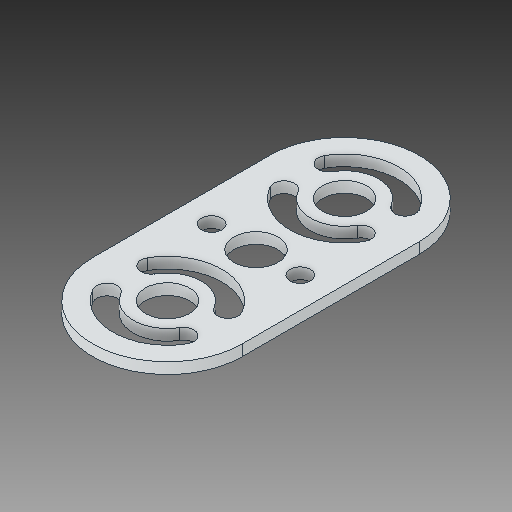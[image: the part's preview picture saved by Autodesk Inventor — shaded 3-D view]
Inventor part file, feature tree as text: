
AUTODESK INVENTOR PART (.ipt)
format: ipt  version: 2018 (Build 220112000, 112)  size: 167,936 bytes
history: native  units: in
note: dims shown in document units (in); Inventor stores cm internally (conversion verified against a paired STEP export)
features: extrude x1
ambient origin geometry x8: Origin, YZ Plane, XZ Plane, XY Plane, X Axis, Y Axis, Z Axis, Center Point
bodies: Solid1 (feature_tree)
feature tree (1):
  extrude  "Extrude2"  [1 undecoded]
note: 1 required parameter value undecoded (feature->parameter linkage not recoverable at this tier; creation-order binding heuristic only, values carry confidence <= 0.55)
